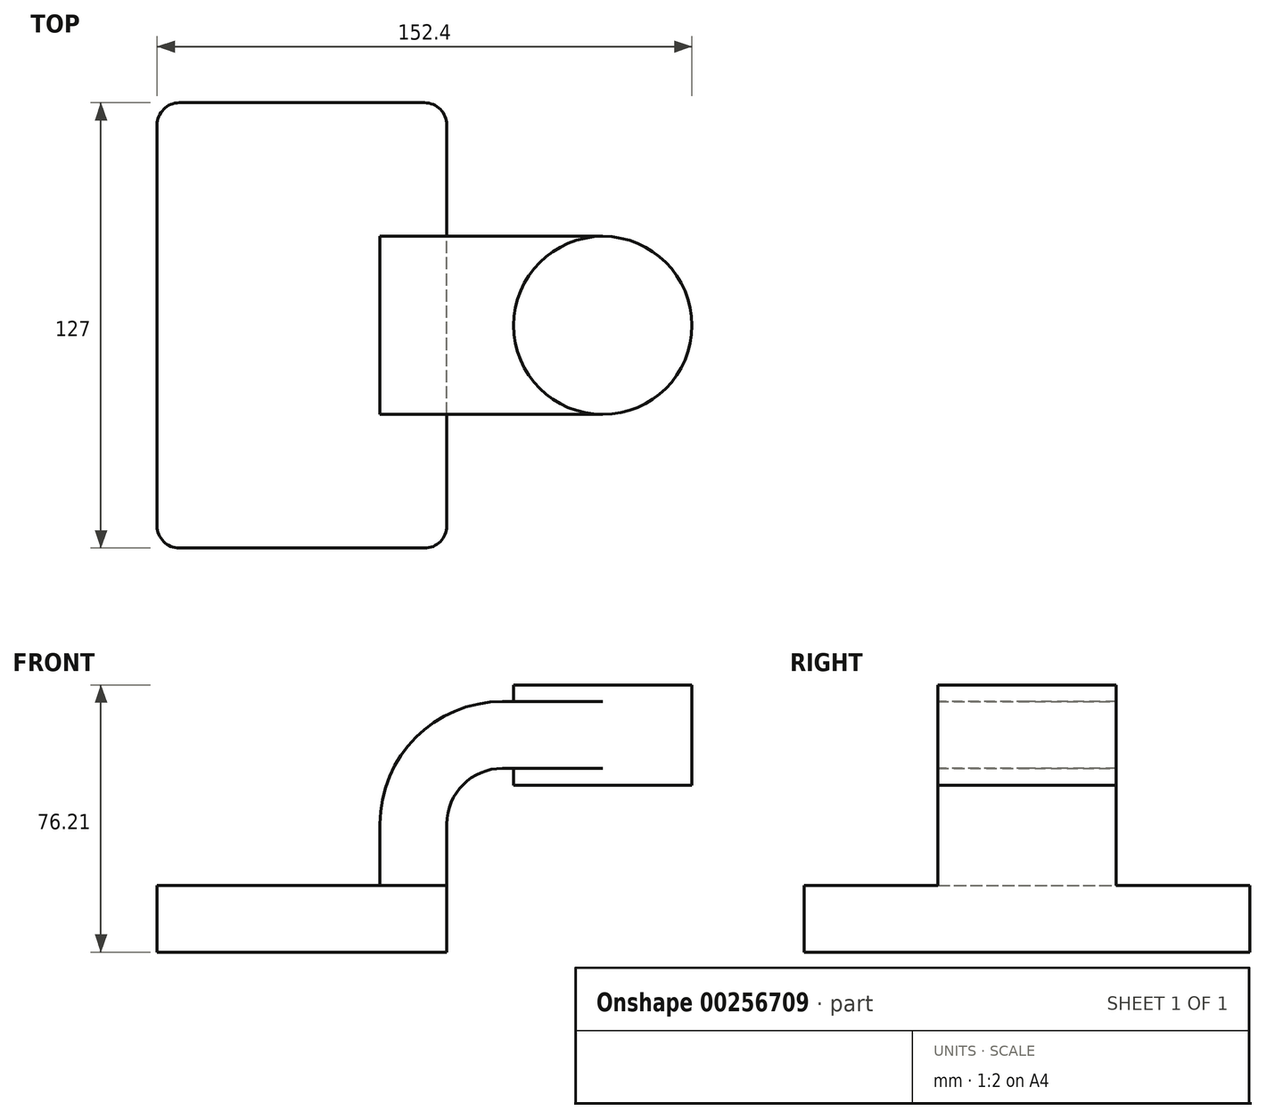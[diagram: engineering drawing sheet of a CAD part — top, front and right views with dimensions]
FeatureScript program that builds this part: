
annotation { "Feature Type Name" : "Feature", "Feature Type Description" : "" }
export const myFeature = defineFeature(function(context is Context, id is Id, definition is map)
    precondition{}
    {
        {
            var Q0;
            Q0=qCreatedBy(makeId("Front.planeOp"),FACE);
            var sketch = newSketch(context, id + "F0", { "sketchPlane" : qUnion([Q0])});
            skLineSegment(sketch, "E0.bottom", {"start": v(41.28, -9.52) * mm, "end": v(-41.28, -9.53) * mm});
            skLineSegment(sketch, "E0.top", {"start": v(41.28, 9.53) * mm, "end": v(-41.28, 9.53) * mm});
            skLineSegment(sketch, "E0.left", {"start": v(41.28, -9.52) * mm, "end": v(41.28, 9.53) * mm});
            skLineSegment(sketch, "E0.right", {"start": v(-41.28, -9.53) * mm, "end": v(-41.28, 9.53) * mm});
            skPoint(sketch, "E0.middle", {"position": v(0, 0) * mm});
            skLineSegment(sketch, "E1.bottom", {"start": v(60.32, 38.1) * mm, "end": v(111.12, 38.1) * mm});
            skLineSegment(sketch, "E1.top", {"start": v(60.32, 66.68) * mm, "end": v(111.12, 66.68) * mm});
            skLineSegment(sketch, "E1.left", {"start": v(60.32, 38.1) * mm, "end": v(60.32, 66.68) * mm});
            skLineSegment(sketch, "E1.right", {"start": v(111.12, 38.1) * mm, "end": v(111.12, 66.68) * mm});
            skPoint(sketch, "E1.middle", {"position": v(85.72, 52.39) * mm});
            skLineSegment(sketch, "E2", {"start": v(41.28, 9.53) * mm, "end": v(41.28, 27) * mm});
            skArc(sketch, "E3", {"start": v(41.27, 27) * mm, "mid": v(45.92, 38.23) * mm, "end": v(57.15, 42.88) * mm});
            skLineSegment(sketch, "E4", {"start": v(57.15, 42.88) * mm, "end": v(91.62, 42.88) * mm});
            skLineSegment(sketch, "E5.0", {"start": v(57.15, 61.93) * mm, "end": v(91.62, 61.93) * mm});
            skArc(sketch, "E5.1", {"start": v(22.23, 27) * mm, "mid": v(32.45, 51.7) * mm, "end": v(57.15, 61.93) * mm});
            skLineSegment(sketch, "E5.2", {"start": v(22.22, 9.53) * mm, "end": v(22.22, 27) * mm});
            skLineSegment(sketch, "E6", {"start": v(85.72, 38.1) * mm, "end": v(85.72, 66.68) * mm});
            skFitSpline(sketch, "E7", {"points": [v(-41.28, 9.52) * mm, v(57.15, 61.93) * mm], "startDerivative": vector(24.45, 131.63) * mm, "endDerivative": vector(126.04, -4.42) * mm});
            skSolve(sketch);
        }
        {
            var Q0;
            Q0=makeQuery(id+"F0.imprint","IMPRINT",FACE,{"disambiguationData":[TD([[makeQuery(id+"F0.imprint","IMPRINT",EDGE,{"derivedFrom":sQuery(id+"F0.wireOp",EDGE,"E0.bottom")}),-1.0]])]});
            extrude(context, id + "F1", {"entities" : qUnion([Q0]), "endBound" : BoundingType.SYMMETRIC, "depth" : 127 * mm});
        }
        {
            var Q0;
            {var subQ1=sQuery(id+"F0.wireOp",EDGE,"E2");Q0=makeQuery(id+"F0.imprint","IMPRINT",FACE,{"disambiguationData":[TD([[makeQuery(id+"F0.imprint","IMPRINT",EDGE,{"derivedFrom":subQ1}),1.0]])]});}
            var Q1;
            {var subQ0=sQuery(id+"F0.wireOp",EDGE,"E4");var subQ1=sQuery(id+"F0.wireOp",EDGE,"E1.left");var subQ2=makeQuery(id+"F0.imprint","INTERSECT",VERTEX,{"derivedFrom":[subQ1,subQ0]});Q1=makeQuery(id+"F0.imprint","IMPRINT",FACE,{"disambiguationData":[TD([[makeQuery(id+"F0.imprint","IMPRINT",EDGE,{"disambiguationData":[TD([[subQ2,-1.0]])],"derivedFrom":subQ1}),-1.0]])]});}
            extrude(context, id + "F2", {"entities" : qUnion([Q0, Q1]), "operationType" : NewBodyOperationType.ADD, "endBound" : BoundingType.SYMMETRIC, "depth" : 50.8 * mm});
        }
        {
            var Q0;
            Q0=makeQuery(id+"F0.imprint","IMPRINT",FACE,{"disambiguationData":[TD([[makeQuery(id+"F0.imprint","IMPRINT",EDGE,{"derivedFrom":sQuery(id+"F0.wireOp",EDGE,"E5.1")}),1.0]])]});
            extrude(context, id + "F3", {"entities" : qUnion([Q0]), "operationType" : NewBodyOperationType.ADD, "endBound" : BoundingType.SYMMETRIC, "depth" : 15.88 * mm});
        }
        {
            var Q0;
            {var subQ0=sQuery(id+"F0.wireOp",EDGE,"E1.right");Q0=makeQuery(id+"F0.imprint","IMPRINT",FACE,{"disambiguationData":[TD([[makeQuery(id+"F0.imprint","IMPRINT",EDGE,{"derivedFrom":subQ0}),1.0]])]});}
            var Q1;
            Q1=sQuery(id+"F0.wireOp",EDGE,"E6");
            revolve(context, id + "F4", {"operationType" : NewBodyOperationType.ADD, "entities" : qUnion([Q0]), "axis" : qUnion([Q1]), "revolveType" : RevolveType.FULL});
        }
        {
            var Q0;
            Q0=makeQuery(id+"F1.opExtrude","CAP_EDGE",EDGE,{"disambiguationData":[OSD([sQuery(id+"F0.wireOp",EDGE,"E0.left")])],"isStart":true});
            var Q1;
            Q1=makeQuery(id+"F1.opExtrude","CAP_EDGE",EDGE,{"disambiguationData":[OSD([sQuery(id+"F0.wireOp",EDGE,"E0.right")])],"isStart":true});
            var Q2;
            Q2=makeQuery(id+"F1.opExtrude","CAP_EDGE",EDGE,{"disambiguationData":[OSD([sQuery(id+"F0.wireOp",EDGE,"E0.right")])],"isStart":false});
            var Q3;
            Q3=makeQuery(id+"F1.opExtrude","CAP_EDGE",EDGE,{"disambiguationData":[OSD([sQuery(id+"F0.wireOp",EDGE,"E0.left")])],"isStart":false});
            fillet(context, id + "F5", {"entities" : qUnion([Q0, Q1, Q2, Q3]), "radius" : 6.35 * mm, "tangentPropagation" : true, "allowEdgeOverflow" : false});
        }
    });
